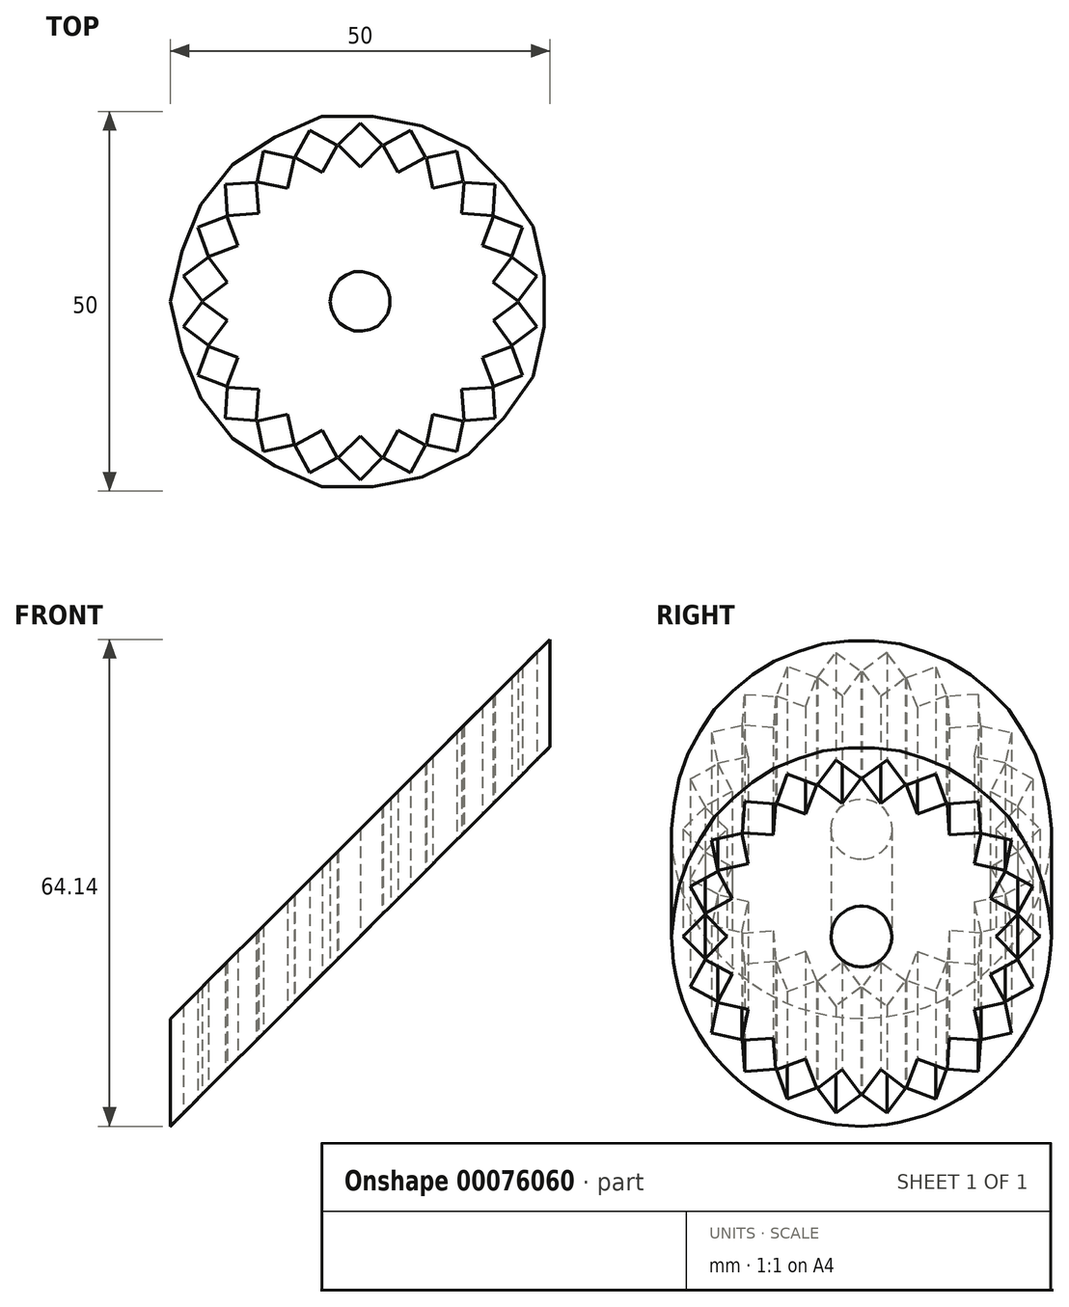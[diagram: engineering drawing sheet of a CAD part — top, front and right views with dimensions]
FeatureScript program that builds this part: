
annotation { "Feature Type Name" : "Feature", "Feature Type Description" : "" }
export const myFeature = defineFeature(function(context is Context, id is Id, definition is map)
    precondition{}
    {
        {
            var Q0;
            Q0=qCreatedBy(makeId("Top.planeOp"),FACE);
            var sketch = newSketch(context, id + "F0", { "sketchPlane" : qUnion([Q0])});
            skCircle(sketch, "E0", {"center": v(0, 0) * mm, "radius": 25 * mm});
            skLineSegment(sketch, "E1", {"start": v(0, 23.5) * mm, "end": v(-2.9, 20.6) * mm});
            skLineSegment(sketch, "E2", {"start": v(-2.9, 20.6) * mm, "end": v(0, 17.7) * mm});
            skLineSegment(sketch, "E3", {"start": v(0, 17.7) * mm, "end": v(2.9, 20.6) * mm});
            skLineSegment(sketch, "E4", {"start": v(2.9, 20.6) * mm, "end": v(0, 23.5) * mm});
            skLineSegment(sketch, "E5", {"start": v(0, 0) * mm, "end": v(-3.56, 24.75) * mm, "construction": true});
            skLineSegment(sketch, "E6", {"start": v(0, 0) * mm, "end": v(3.56, 24.75) * mm, "construction": true});
            skLineSegment(sketch, "E7", {"start": v(1.43, 9.92) * mm, "end": v(0, 9.92) * mm});
            skLineSegment(sketch, "E8", {"start": v(0, 9.92) * mm, "end": v(-1.43, 9.92) * mm});
            skLineSegment(sketch, "E9.MirrorCS", {"start": v(0, 0) * mm, "end": v(-10.39, 22.74) * mm, "construction": true});
            skLineSegment(sketch, "E10.MirrorCS", {"start": v(-6.62, 22.55) * mm, "end": v(-3.02, 20.58) * mm});
            skLineSegment(sketch, "E11.MirrorCS", {"start": v(-8.59, 18.95) * mm, "end": v(-6.62, 22.55) * mm});
            skLineSegment(sketch, "E12.MirrorCS", {"start": v(-4.99, 16.98) * mm, "end": v(-8.59, 18.95) * mm});
            skLineSegment(sketch, "E13.MirrorCS", {"start": v(-3.02, 20.58) * mm, "end": v(-4.99, 16.98) * mm});
            skLineSegment(sketch, "E14.MirrorCS", {"start": v(-13.38, 11.6) * mm, "end": v(-17.47, 11.3) * mm});
            skLineSegment(sketch, "E15.MirrorCS", {"start": v(-13.67, 15.68) * mm, "end": v(-13.38, 11.6) * mm});
            skLineSegment(sketch, "E16.MirrorCS", {"start": v(-13.58, 15.76) * mm, "end": v(-9.57, 14.9) * mm});
            skLineSegment(sketch, "E17.MirrorCS", {"start": v(-9.57, 14.9) * mm, "end": v(-8.7, 18.9) * mm});
            skLineSegment(sketch, "E18.MirrorCS", {"start": v(-8.7, 18.9) * mm, "end": v(-12.7, 19.77) * mm});
            skLineSegment(sketch, "E19.MirrorCS", {"start": v(-12.7, 19.77) * mm, "end": v(-13.58, 15.76) * mm});
            skLineSegment(sketch, "E20.MirrorCS", {"start": v(-17.76, 15.39) * mm, "end": v(-13.67, 15.68) * mm});
            skLineSegment(sketch, "E21.MirrorCS", {"start": v(-17.47, 11.3) * mm, "end": v(-17.76, 15.39) * mm});
            skLineSegment(sketch, "E22.MirrorCS", {"start": v(0, 0) * mm, "end": v(-21.03, 13.52) * mm, "construction": true});
            skLineSegment(sketch, "E23.MirrorCS", {"start": v(-19.98, -5.8) * mm, "end": v(-17.52, -2.52) * mm});
            skLineSegment(sketch, "E24.MirrorCS", {"start": v(-19.98, 5.8) * mm, "end": v(-17.52, 2.52) * mm});
            skLineSegment(sketch, "E25.MirrorCS", {"start": v(-17.52, -2.52) * mm, "end": v(-20.8, -0.06) * mm});
            skLineSegment(sketch, "E26.MirrorCS", {"start": v(-20.8, 0.06) * mm, "end": v(-23.26, 3.34) * mm});
            skLineSegment(sketch, "E27.MirrorCS", {"start": v(-21.38, 9.76) * mm, "end": v(-19.94, 5.92) * mm});
            skLineSegment(sketch, "E28.MirrorCS", {"start": v(-17.52, 2.52) * mm, "end": v(-20.8, 0.06) * mm});
            skLineSegment(sketch, "E29.MirrorCS", {"start": v(-17.53, -11.2) * mm, "end": v(-21.38, -9.76) * mm});
            skLineSegment(sketch, "E30.MirrorCS", {"start": v(-19.94, -5.92) * mm, "end": v(-16.1, -7.35) * mm});
            skLineSegment(sketch, "E31.MirrorCS", {"start": v(-23.26, 3.34) * mm, "end": v(-19.98, 5.8) * mm});
            skLineSegment(sketch, "E32.MirrorCS", {"start": v(-21.38, -9.76) * mm, "end": v(-19.94, -5.92) * mm});
            skLineSegment(sketch, "E33.MirrorCS", {"start": v(-20.8, -0.06) * mm, "end": v(-23.26, -3.35) * mm});
            skLineSegment(sketch, "E34.MirrorCS", {"start": v(-23.26, -3.35) * mm, "end": v(-19.98, -5.8) * mm});
            skLineSegment(sketch, "E35.MirrorCS", {"start": v(-16.1, -7.35) * mm, "end": v(-17.53, -11.2) * mm});
            skLineSegment(sketch, "E36.MirrorCS", {"start": v(-19.94, 5.92) * mm, "end": v(-16.1, 7.35) * mm});
            skLineSegment(sketch, "E37.MirrorCS", {"start": v(-16.1, 7.35) * mm, "end": v(-17.54, 11.2) * mm});
            skLineSegment(sketch, "E38.MirrorCS", {"start": v(-17.54, 11.2) * mm, "end": v(-21.38, 9.76) * mm});
            skLineSegment(sketch, "E39.MirrorCS", {"start": v(0, 0) * mm, "end": v(-21.03, -13.52) * mm, "construction": true});
            skLineSegment(sketch, "E40.MirrorCS", {"start": v(17.54, -11.2) * mm, "end": v(16.1, -7.35) * mm});
            skLineSegment(sketch, "E41.MirrorCS", {"start": v(17.47, -11.3) * mm, "end": v(13.38, -11.6) * mm});
            skLineSegment(sketch, "E42.MirrorCS", {"start": v(13.38, -11.6) * mm, "end": v(13.67, -15.68) * mm});
            skLineSegment(sketch, "E43.MirrorCS", {"start": v(9.03, -4.12) * mm, "end": v(8.43, -5.42) * mm});
            skLineSegment(sketch, "E44.MirrorCS", {"start": v(9.62, -2.82) * mm, "end": v(9.03, -4.12) * mm});
            skLineSegment(sketch, "E45.MirrorCS", {"start": v(0, -23.5) * mm, "end": v(-2.9, -20.6) * mm});
            skLineSegment(sketch, "E46.MirrorCS", {"start": v(-13.58, -15.76) * mm, "end": v(-9.57, -14.9) * mm});
            skLineSegment(sketch, "E47.MirrorCS", {"start": v(6.62, -22.55) * mm, "end": v(8.59, -18.95) * mm});
            skLineSegment(sketch, "E48.MirrorCS", {"start": v(-2.9, -20.6) * mm, "end": v(0, -17.7) * mm});
            skLineSegment(sketch, "E49.MirrorCS", {"start": v(-17.47, -11.3) * mm, "end": v(-17.76, -15.4) * mm});
            skLineSegment(sketch, "E50.MirrorCS", {"start": v(8.7, -18.9) * mm, "end": v(9.57, -14.9) * mm});
            skLineSegment(sketch, "E51.MirrorCS", {"start": v(-17.76, -15.4) * mm, "end": v(-13.67, -15.68) * mm});
            skLineSegment(sketch, "E52.MirrorCS", {"start": v(-3.02, -20.58) * mm, "end": v(-4.99, -16.98) * mm});
            skLineSegment(sketch, "E53.MirrorCS", {"start": v(-13.67, -15.68) * mm, "end": v(-13.38, -11.6) * mm});
            skLineSegment(sketch, "E54.MirrorCS", {"start": v(3.02, -20.58) * mm, "end": v(6.62, -22.55) * mm});
            skLineSegment(sketch, "E55.MirrorCS", {"start": v(0, -17.7) * mm, "end": v(2.9, -20.6) * mm});
            skLineSegment(sketch, "E56.MirrorCS", {"start": v(-9.57, -14.9) * mm, "end": v(-8.7, -18.9) * mm});
            skLineSegment(sketch, "E57.MirrorCS", {"start": v(9.57, -14.9) * mm, "end": v(13.58, -15.76) * mm});
            skLineSegment(sketch, "E58.MirrorCS", {"start": v(-8.7, -18.9) * mm, "end": v(-12.7, -19.77) * mm});
            skLineSegment(sketch, "E59.MirrorCS", {"start": v(8.59, -18.95) * mm, "end": v(4.99, -16.98) * mm});
            skLineSegment(sketch, "E60.MirrorCS", {"start": v(-6.62, -22.55) * mm, "end": v(-3.02, -20.58) * mm});
            skLineSegment(sketch, "E61.MirrorCS", {"start": v(21.38, -9.76) * mm, "end": v(17.54, -11.2) * mm});
            skLineSegment(sketch, "E62.MirrorCS", {"start": v(-12.7, -19.77) * mm, "end": v(-13.58, -15.76) * mm});
            skLineSegment(sketch, "E63.MirrorCS", {"start": v(13.58, -15.76) * mm, "end": v(12.7, -19.77) * mm});
            skLineSegment(sketch, "E64.MirrorCS", {"start": v(16.1, -7.35) * mm, "end": v(19.94, -5.92) * mm});
            skLineSegment(sketch, "E65.MirrorCS", {"start": v(17.76, -15.39) * mm, "end": v(17.47, -11.3) * mm});
            skLineSegment(sketch, "E66.MirrorCS", {"start": v(-13.38, -11.6) * mm, "end": v(-17.47, -11.3) * mm});
            skLineSegment(sketch, "E67.MirrorCS", {"start": v(-8.58, -18.95) * mm, "end": v(-6.62, -22.55) * mm});
            skLineSegment(sketch, "E68.MirrorCS", {"start": v(4.99, -16.98) * mm, "end": v(3.02, -20.58) * mm});
            skLineSegment(sketch, "E69.MirrorCS", {"start": v(13.67, -15.68) * mm, "end": v(17.76, -15.39) * mm});
            skLineSegment(sketch, "E70.MirrorCS", {"start": v(2.9, -20.6) * mm, "end": v(0, -23.5) * mm});
            skLineSegment(sketch, "E71.MirrorCS", {"start": v(12.7, -19.77) * mm, "end": v(8.7, -18.9) * mm});
            skLineSegment(sketch, "E72.MirrorCS", {"start": v(19.94, -5.92) * mm, "end": v(21.38, -9.76) * mm});
            skLineSegment(sketch, "E73.MirrorCS", {"start": v(-4.99, -16.98) * mm, "end": v(-8.58, -18.95) * mm});
            skLineSegment(sketch, "E74.MirrorCS", {"start": v(0, 0) * mm, "end": v(16.37, -18.9) * mm, "construction": true});
            skLineSegment(sketch, "E75.MirrorCS", {"start": v(0, 0) * mm, "end": v(3.56, -24.75) * mm, "construction": true});
            skLineSegment(sketch, "E76.MirrorCS", {"start": v(0, 0) * mm, "end": v(23.99, -7.04) * mm, "construction": true});
            skLineSegment(sketch, "E77.MirrorCS", {"start": v(0, 0) * mm, "end": v(21.03, -13.51) * mm, "construction": true});
            skLineSegment(sketch, "E78.MirrorCS", {"start": v(13.67, 15.68) * mm, "end": v(17.76, 15.4) * mm});
            skLineSegment(sketch, "E79.MirrorCS", {"start": v(13.57, 15.76) * mm, "end": v(12.7, 19.77) * mm});
            skLineSegment(sketch, "E80.MirrorCS", {"start": v(19.94, 5.92) * mm, "end": v(21.38, 9.76) * mm});
            skLineSegment(sketch, "E81.MirrorCS", {"start": v(17.76, 15.4) * mm, "end": v(17.47, 11.3) * mm});
            skLineSegment(sketch, "E82.MirrorCS", {"start": v(9.57, 14.9) * mm, "end": v(13.57, 15.76) * mm});
            skLineSegment(sketch, "E83.MirrorCS", {"start": v(21.38, 9.76) * mm, "end": v(17.53, 11.2) * mm});
            skLineSegment(sketch, "E84.MirrorCS", {"start": v(17.52, -2.52) * mm, "end": v(19.98, -5.8) * mm});
            skLineSegment(sketch, "E85.MirrorCS", {"start": v(8.7, 18.9) * mm, "end": v(9.57, 14.9) * mm});
            skLineSegment(sketch, "E86.MirrorCS", {"start": v(20.8, -0.06) * mm, "end": v(17.52, -2.52) * mm});
            skLineSegment(sketch, "E87.MirrorCS", {"start": v(19.98, -5.8) * mm, "end": v(23.26, -3.34) * mm});
            skLineSegment(sketch, "E88.MirrorCS", {"start": v(23.26, 3.35) * mm, "end": v(20.8, 0.06) * mm});
            skLineSegment(sketch, "E89.MirrorCS", {"start": v(12.7, 19.77) * mm, "end": v(8.7, 18.9) * mm});
            skLineSegment(sketch, "E90.MirrorCS", {"start": v(8.58, 18.95) * mm, "end": v(4.98, 16.99) * mm});
            skLineSegment(sketch, "E91.MirrorCS", {"start": v(17.53, 11.2) * mm, "end": v(16.1, 7.36) * mm});
            skLineSegment(sketch, "E92.MirrorCS", {"start": v(13.38, 11.6) * mm, "end": v(13.67, 15.68) * mm});
            skLineSegment(sketch, "E93.MirrorCS", {"start": v(23.26, -3.34) * mm, "end": v(20.8, -0.06) * mm});
            skLineSegment(sketch, "E94.MirrorCS", {"start": v(4.98, 16.99) * mm, "end": v(3.02, 20.58) * mm});
            skLineSegment(sketch, "E95.MirrorCS", {"start": v(9.82, -1.41) * mm, "end": v(10.02, 0) * mm});
            skLineSegment(sketch, "E96.MirrorCS", {"start": v(17.47, 11.3) * mm, "end": v(13.38, 11.6) * mm});
            skLineSegment(sketch, "E97.MirrorCS", {"start": v(16.1, 7.36) * mm, "end": v(19.94, 5.92) * mm});
            skLineSegment(sketch, "E98.MirrorCS", {"start": v(19.98, 5.8) * mm, "end": v(23.26, 3.35) * mm});
            skLineSegment(sketch, "E99.MirrorCS", {"start": v(3.02, 20.58) * mm, "end": v(6.62, 22.55) * mm});
            skLineSegment(sketch, "E100.MirrorCS", {"start": v(6.62, 22.55) * mm, "end": v(8.58, 18.95) * mm});
            skLineSegment(sketch, "E101.MirrorCS", {"start": v(17.52, 2.52) * mm, "end": v(19.98, 5.8) * mm});
            skLineSegment(sketch, "E102.MirrorCS", {"start": v(0, 0) * mm, "end": v(23.99, 7.05) * mm, "construction": true});
            skLineSegment(sketch, "E103.MirrorCS", {"start": v(20.8, 0.06) * mm, "end": v(17.52, 2.52) * mm});
            skLineSegment(sketch, "E104.MirrorCS", {"start": v(0, 0) * mm, "end": v(25, 0) * mm, "construction": true});
            skLineSegment(sketch, "E105.MirrorCS", {"start": v(0, 0) * mm, "end": v(16.37, 18.9) * mm, "construction": true});
            skSolve(sketch);
        }
        {
            var Q0;
            Q0 = qSketchRegion(id + "F0", true);
            extrude(context, id + "F1", {"entities" : qUnion([Q0]), "depth" : 140 * mm, "hasSecondDirection" : true, "secondDirectionOppositeDirection" : true, "secondDirectionDepth" : 140 * mm});
        }
        {
            var Q0;
            Q0=qCreatedBy(makeId("Front.planeOp"),FACE);
            var sketch = newSketch(context, id + "F2", { "sketchPlane" : qUnion([Q0])});
            skLineSegment(sketch, "E106", {"start": v(-68.42, 0) * mm, "end": v(91.57, 159.99) * mm});
            skLineSegment(sketch, "E107", {"start": v(91.57, 159.99) * mm, "end": v(-70.22, 159.99) * mm});
            skLineSegment(sketch, "E108", {"start": v(-70.22, 159.99) * mm, "end": v(-68.42, 0) * mm});
            skLineSegment(sketch, "E109", {"start": v(-61.35, 0) * mm, "end": v(60.82, 122.16) * mm});
            skLineSegment(sketch, "E110.MirrorCS", {"start": v(-61.35, -7.07) * mm, "end": v(98.64, 152.92) * mm});
            skLineSegment(sketch, "E111", {"start": v(-61.35, -7.07) * mm, "end": v(-72.75, -18.47) * mm});
            skLineSegment(sketch, "E112", {"start": v(-72.75, -18.47) * mm, "end": v(-64, -174.67) * mm});
            skLineSegment(sketch, "E113", {"start": v(-64, -174.67) * mm, "end": v(77.08, -174.67) * mm});
            skLineSegment(sketch, "E114", {"start": v(77.08, -174.67) * mm, "end": v(98.64, 152.92) * mm});
            skSolve(sketch);
        }
        {
            var Q0;
            Q0=makeQuery(id+"F2.imprint","IMPRINT",FACE,{"disambiguationData":[TD([[makeQuery(id+"F2.imprint","IMPRINT",EDGE,{"derivedFrom":sQuery(id+"F2.wireOp",EDGE,"E110.MirrorCS")}),-1.0]])]});
            var Q1;
            Q1=makeQuery(id+"F2.imprint","IMPRINT",FACE,{"disambiguationData":[TD([[makeQuery(id+"F2.imprint","IMPRINT",EDGE,{"derivedFrom":sQuery(id+"F2.wireOp",EDGE,"E106")}),1.0]])]});
            extrude(context, id + "F3", {"entities" : qUnion([Q0, Q1]), "operationType" : NewBodyOperationType.REMOVE, "depth" : 70 * mm, "hasSecondDirection" : true, "secondDirectionOppositeDirection" : true, "secondDirectionDepth" : 70 * mm});
        }
        {
            var Q0;
            Q0=qCreatedBy(makeId("Top.planeOp"),FACE);
            var sketch = newSketch(context, id + "F4", { "sketchPlane" : qUnion([Q0])});
            skCircle(sketch, "E115", {"center": v(0, 0) * mm, "radius": 4 * mm});
            skSolve(sketch);
        }
        {
            var Q0;
            Q0=makeQuery(id+"F4.imprint","IMPRINT",FACE,{"disambiguationData":[TD([[makeQuery(id+"F4.imprint","IMPRINT",EDGE,{"derivedFrom":sQuery(id+"F4.wireOp",EDGE,"E115")}),1.0]])]});
            extrude(context, id + "F5", {"entities" : qUnion([Q0]), "operationType" : NewBodyOperationType.REMOVE, "depth" : 100 * mm});
        }
    });
